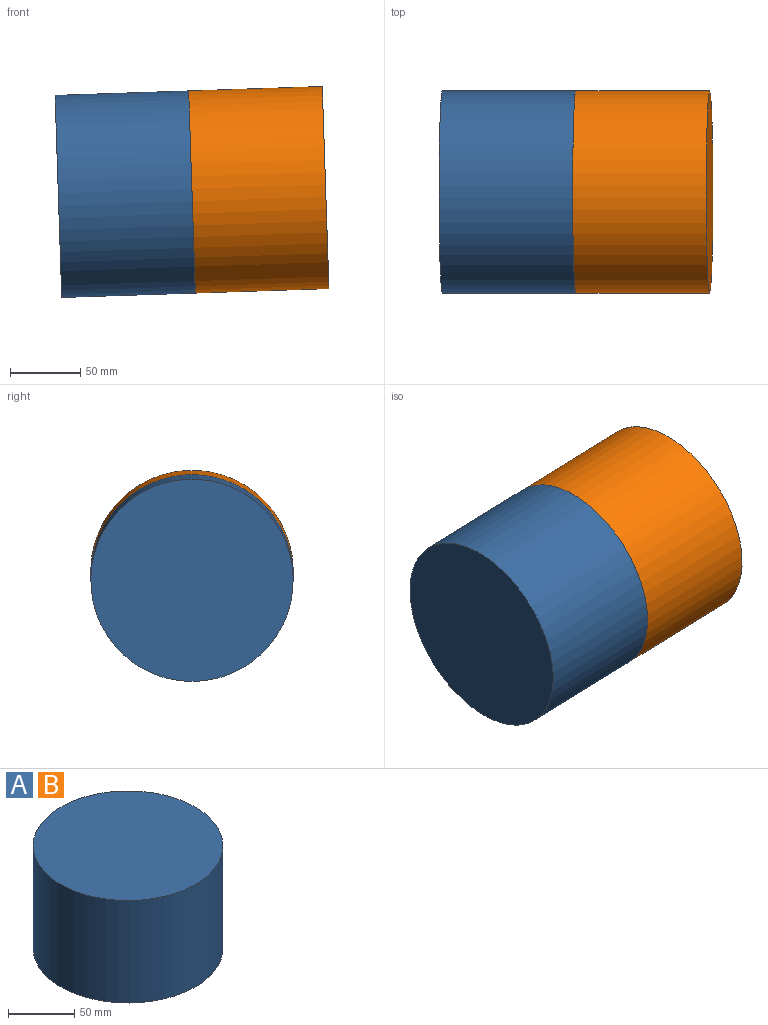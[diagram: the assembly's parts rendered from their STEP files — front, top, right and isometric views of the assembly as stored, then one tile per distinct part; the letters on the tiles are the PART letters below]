
ASSEMBLY  parts=2 mates=1
PART A: 3 faces, bbox 143.9x143.9x95 mm
  f0: cylinder r=71.94mm len=143.87mm, axis (0,0,-1), area 42938.6mm2, adj f1,f2
  f1: plane 143.87x143.87mm, normal (0,0,1), area 16256.9mm2, adj f0
  f2: plane 143.87x143.87mm, normal (0,0,-1), area 16256.9mm2, adj f0
PART B: same geometry as A
PLACE A rot(axis=(0,1,0),88.1deg) t=(-125.75,-87.83,150.98)mm
PLACE B rot(axis=(0,1,0),88.1deg) t=(-30.8,-87.83,154.13)mm
MATE cylindrical A.f0 <-> B.f0  axis (1,0,0.03) through (-30.81,-87.83,154.13)mm
